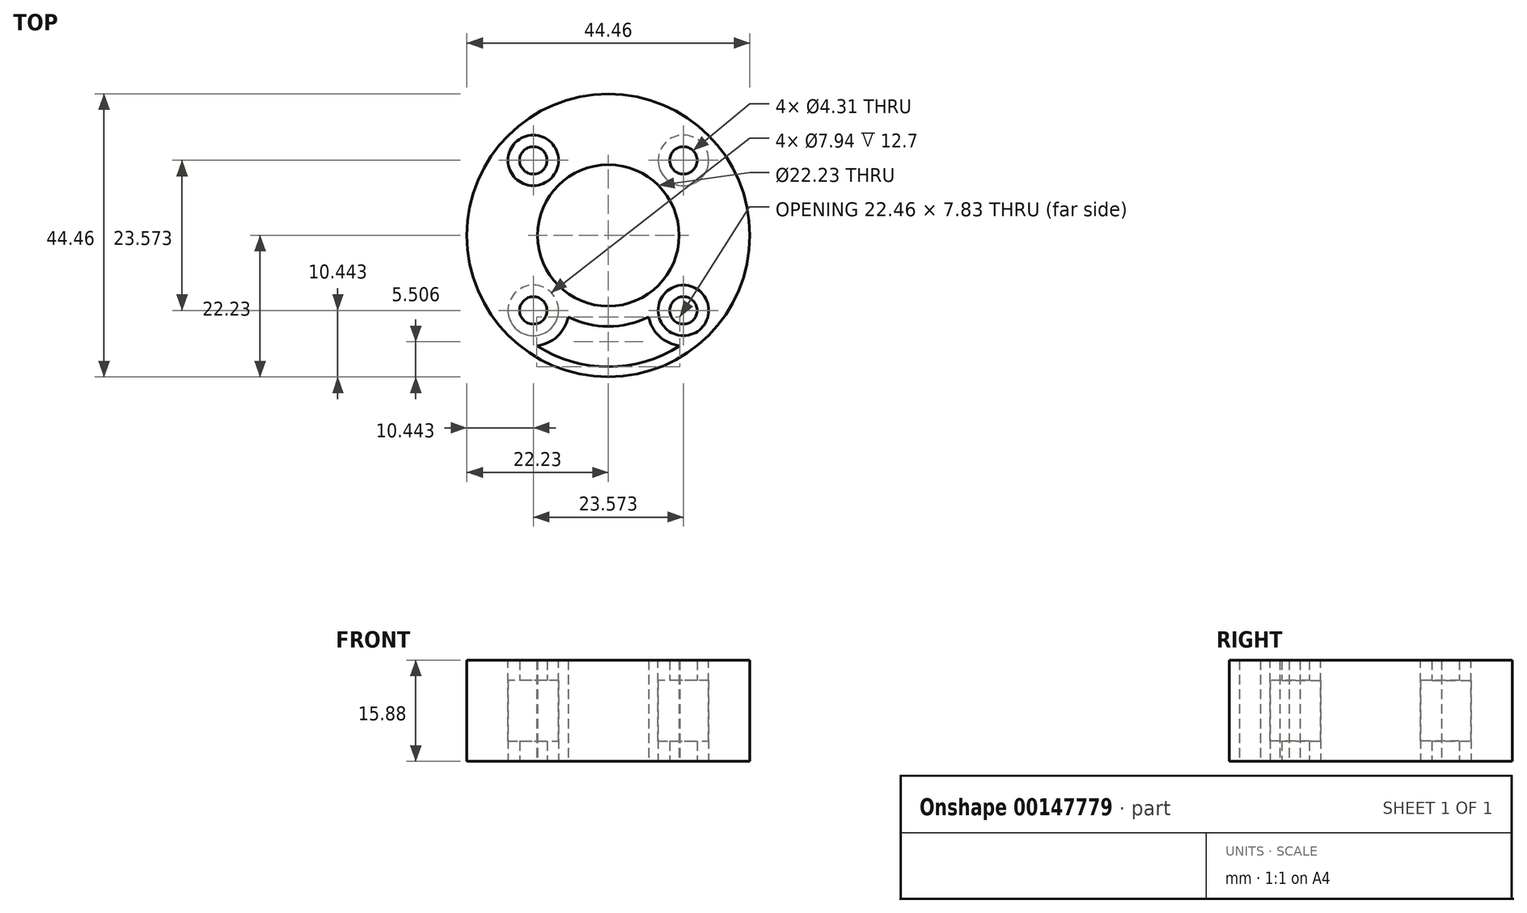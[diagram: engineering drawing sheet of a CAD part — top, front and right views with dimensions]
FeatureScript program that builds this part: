
annotation { "Feature Type Name" : "Feature", "Feature Type Description" : "" }
export const myFeature = defineFeature(function(context is Context, id is Id, definition is map)
    precondition{}
    {
        {
            var Q0;
            Q0=qCreatedBy(makeId("Top.planeOp"),FACE);
            var sketch = newSketch(context, id + "F0", { "sketchPlane" : qUnion([Q0])});
            skCircle(sketch, "E0", {"center": v(0, 0) * mm, "radius": 11.11 * mm});
            skLineSegment(sketch, "E1.bottom", {"start": v(11.79, 11.79) * mm, "end": v(-11.79, 11.79) * mm, "construction": true});
            skLineSegment(sketch, "E1.top", {"start": v(11.79, -11.79) * mm, "end": v(-11.79, -11.79) * mm, "construction": true});
            skLineSegment(sketch, "E1.left", {"start": v(11.79, 11.79) * mm, "end": v(11.79, -11.79) * mm, "construction": true});
            skLineSegment(sketch, "E1.right", {"start": v(-11.79, 11.79) * mm, "end": v(-11.79, -11.79) * mm, "construction": true});
            skCircle(sketch, "E2", {"center": v(-11.79, 11.79) * mm, "radius": 5.56 * mm, "construction": true});
            skLineSegment(sketch, "E3", {"start": v(0, 0) * mm, "end": v(0, 11.11) * mm});
            skCircle(sketch, "E4", {"center": v(-11.79, 11.79) * mm, "radius": 2.15 * mm});
            skCircle(sketch, "E5", {"center": v(-11.79, -11.79) * mm, "radius": 2.15 * mm});
            skCircle(sketch, "E6", {"center": v(11.79, -11.79) * mm, "radius": 2.15 * mm});
            skCircle(sketch, "E7", {"center": v(11.79, 11.79) * mm, "radius": 2.15 * mm});
            skCircle(sketch, "E8", {"center": v(0, 0) * mm, "radius": 22.23 * mm});
            skSolve(sketch);
        }
        {
            var Q0;
            Q0=qSketchRegion(id+"F0",true);
            extrude(context, id + "F1", {"entities" : qUnion([Q0]), "depth" : 15.88 * mm});
        }
        {
            var Q0;
            Q0=makeQuery(id+"F1.opExtrude","CAP_FACE",FACE,{"disambiguationData":[OSD([sQuery(id+"F0.wireOp",EDGE,"E0"),sQuery(id+"F0.wireOp",EDGE,"E4"),sQuery(id+"F0.wireOp",EDGE,"E5"),sQuery(id+"F0.wireOp",EDGE,"E6"),sQuery(id+"F0.wireOp",EDGE,"E7"),sQuery(id+"F0.wireOp",EDGE,"E8")])],"isStart":true});
            cPlane(context, id + "F2", {"entities" : qUnion([Q0]), "cplaneType" : CPlaneType.OFFSET, "offset" : 3.17 * mm, "oppositeDirection" : true, "width" : 152.4 * mm, "height" : 152.4 * mm});
        }
        {
            var Q0;
            Q0=makeQuery(id+"F1.opExtrude","CAP_FACE",FACE,{"disambiguationData":[OSD([sQuery(id+"F0.wireOp",EDGE,"E0"),sQuery(id+"F0.wireOp",EDGE,"E4"),sQuery(id+"F0.wireOp",EDGE,"E5"),sQuery(id+"F0.wireOp",EDGE,"E6"),sQuery(id+"F0.wireOp",EDGE,"E7"),sQuery(id+"F0.wireOp",EDGE,"E8")])],"isStart":false});
            cPlane(context, id + "F3", {"entities" : qUnion([Q0]), "cplaneType" : CPlaneType.OFFSET, "offset" : 3.17 * mm, "oppositeDirection" : true, "width" : 152.4 * mm, "height" : 152.4 * mm});
        }
        {
            var Q0;
            Q0=makeQuery(id+"F1.opExtrude","CAP_FACE",FACE,{"disambiguationData":[OSD([sQuery(id+"F0.wireOp",EDGE,"E0"),sQuery(id+"F0.wireOp",EDGE,"E4"),sQuery(id+"F0.wireOp",EDGE,"E5"),sQuery(id+"F0.wireOp",EDGE,"E6"),sQuery(id+"F0.wireOp",EDGE,"E7"),sQuery(id+"F0.wireOp",EDGE,"E8")])],"isStart":true});
            var sketch = newSketch(context, id + "F4", { "sketchPlane" : qUnion([Q0])});
            skCircle(sketch, "E9", {"center": v(11.79, -11.79) * mm, "radius": 3.97 * mm});
            skCircle(sketch, "E10", {"center": v(-11.79, 11.79) * mm, "radius": 3.97 * mm});
            skSolve(sketch);
        }
        {
            var Q0;
            Q0=qSketchRegion(id+"F4",true);
            var Q1;
            Q1=qCreatedBy(id+"F3.planeOp",FACE);
            extrude(context, id + "F5", {"entities" : qUnion([Q0]), "operationType" : NewBodyOperationType.REMOVE, "endBound" : BoundingType.UP_TO_SURFACE, "oppositeDirection" : true, "endBoundEntityFace" : qUnion([Q1]), "depth" : 25.4 * mm});
        }
        {
            var Q0;
            Q0=makeQuery(id+"F1.opExtrude","CAP_FACE",FACE,{"disambiguationData":[OSD([sQuery(id+"F0.wireOp",EDGE,"E0"),sQuery(id+"F0.wireOp",EDGE,"E4"),sQuery(id+"F0.wireOp",EDGE,"E5"),sQuery(id+"F0.wireOp",EDGE,"E6"),sQuery(id+"F0.wireOp",EDGE,"E7"),sQuery(id+"F0.wireOp",EDGE,"E8")])],"isStart":false});
            var sketch = newSketch(context, id + "F6", { "sketchPlane" : qUnion([Q0])});
            skCircle(sketch, "E11", {"center": v(-11.79, 11.79) * mm, "radius": 3.97 * mm});
            skCircle(sketch, "E12", {"center": v(11.79, -11.79) * mm, "radius": 3.97 * mm});
            skSolve(sketch);
        }
        {
            var Q0;
            Q0=qSketchRegion(id+"F6",true);
            var Q1;
            Q1=qCreatedBy(id+"F2.planeOp",FACE);
            extrude(context, id + "F7", {"entities" : qUnion([Q0]), "operationType" : NewBodyOperationType.REMOVE, "endBound" : BoundingType.UP_TO_SURFACE, "oppositeDirection" : true, "endBoundEntityFace" : qUnion([Q1]), "depth" : 25.4 * mm});
        }
        {
            var Q0;
            Q0=makeQuery(id+"F1.opExtrude","CAP_FACE",FACE,{"disambiguationData":[OSD([sQuery(id+"F0.wireOp",EDGE,"E0"),sQuery(id+"F0.wireOp",EDGE,"E4"),sQuery(id+"F0.wireOp",EDGE,"E5"),sQuery(id+"F0.wireOp",EDGE,"E6"),sQuery(id+"F0.wireOp",EDGE,"E7"),sQuery(id+"F0.wireOp",EDGE,"E8")])],"isStart":true});
            var sketch = newSketch(context, id + "F8", { "sketchPlane" : qUnion([Q0])});
            skArc(sketch, "E13", {"start": v(-6.33, 12.81) * mm, "mid": v(-8.03, 15.88) * mm, "end": v(-11.23, 17.31) * mm});
            skArc(sketch, "E14", {"start": v(11.23, 17.31) * mm, "mid": v(0, 20.64) * mm, "end": v(-11.23, 17.31) * mm});
            skArc(sketch, "E15", {"start": v(11.23, 17.31) * mm, "mid": v(8.03, 15.88) * mm, "end": v(6.33, 12.81) * mm});
            skArc(sketch, "E16", {"start": v(6.33, 12.81) * mm, "mid": v(0, 14.29) * mm, "end": v(-6.33, 12.81) * mm});
            skSolve(sketch);
        }
        {
            var Q0;
            Q0=qSketchRegion(id+"F8",true);
            var Q1;
            Q1=makeQuery(id+"F1.opExtrude","CAP_FACE",FACE,{"disambiguationData":[OSD([sQuery(id+"F0.wireOp",EDGE,"E0"),sQuery(id+"F0.wireOp",EDGE,"E4"),sQuery(id+"F0.wireOp",EDGE,"E5"),sQuery(id+"F0.wireOp",EDGE,"E6"),sQuery(id+"F0.wireOp",EDGE,"E7"),sQuery(id+"F0.wireOp",EDGE,"E8")])],"isStart":false});
            extrude(context, id + "F9", {"entities" : qUnion([Q0]), "operationType" : NewBodyOperationType.REMOVE, "endBound" : BoundingType.UP_TO_SURFACE, "oppositeDirection" : true, "endBoundEntityFace" : qUnion([Q1]), "depth" : 25.4 * mm});
        }
    });
